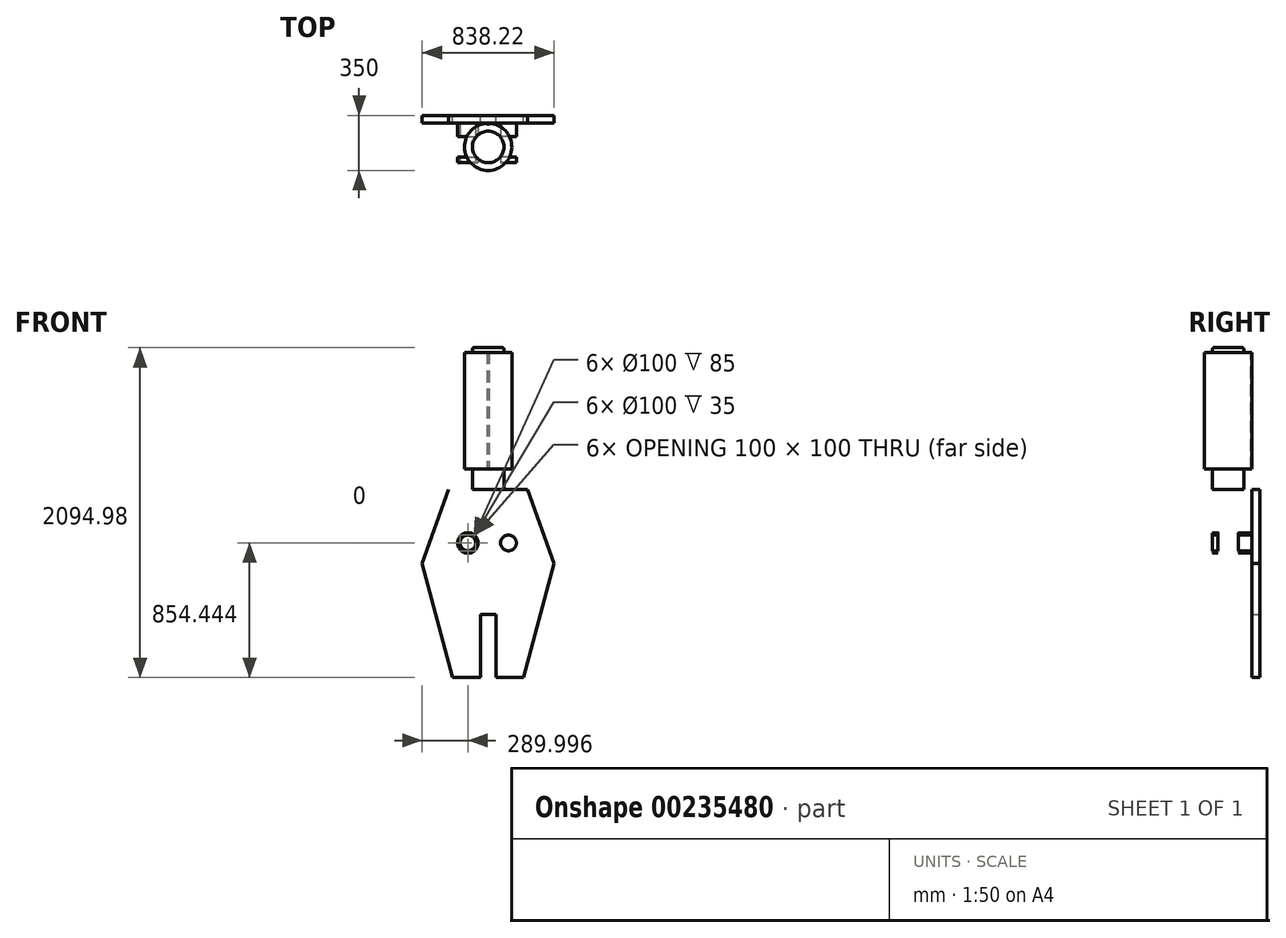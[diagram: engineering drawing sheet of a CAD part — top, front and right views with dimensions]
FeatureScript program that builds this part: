
annotation { "Feature Type Name" : "Feature", "Feature Type Description" : "" }
export const myFeature = defineFeature(function(context is Context, id is Id, definition is map)
    precondition{}
    {
        {
            var Q0;
            Q0=qCreatedBy(makeId("Front.planeOp"),FACE);
            var sketch = newSketch(context, id + "F0", { "sketchPlane" : qUnion([Q0])});
            skLineSegment(sketch, "E0", {"start": v(-250, 794.98) * mm, "end": v(250, 794.98) * mm});
            skLineSegment(sketch, "E1", {"start": v(250, 794.98) * mm, "end": v(419.11, 324.44) * mm});
            skLineSegment(sketch, "E2", {"start": v(419.11, 324.44) * mm, "end": v(225, -400) * mm});
            skLineSegment(sketch, "E3", {"start": v(225, -400) * mm, "end": v(50, -400) * mm});
            skLineSegment(sketch, "E4", {"start": v(-50, -400) * mm, "end": v(-50, 0) * mm});
            skLineSegment(sketch, "E5", {"start": v(0, 0) * mm, "end": v(-50, 0) * mm});
            skLineSegment(sketch, "E6.MirrorCS", {"start": v(-250, 794.98) * mm, "end": v(-419.11, 324.44) * mm});
            skLineSegment(sketch, "E7.MirrorCS", {"start": v(-419.11, 324.44) * mm, "end": v(-225, -400) * mm});
            skLineSegment(sketch, "E8.MirrorCS", {"start": v(-225, -400) * mm, "end": v(-50, -400) * mm});
            skLineSegment(sketch, "E9.MirrorCS", {"start": v(50, -400) * mm, "end": v(50, 0) * mm});
            skLineSegment(sketch, "E10.MirrorCS", {"start": v(0, 0) * mm, "end": v(50, 0) * mm});
            skPoint(sketch, "E11.orphan", {"position": v(50, -400) * mm});
            skSolve(sketch);
        }
        {
            var Q0;
            Q0=makeQuery(id+"F0.imprint","IMPRINT",FACE,{"disambiguationData":[TD([[makeQuery(id+"F0.imprint","IMPRINT",EDGE,{"derivedFrom":sQuery(id+"F0.wireOp",EDGE,"E0")}),-1.0]])]});
            extrude(context, id + "F1", {"entities" : qUnion([Q0]), "endBound" : BoundingType.SYMMETRIC, "depth" : 400 * mm});
        }
        {
            var Q0;
            Q0=makeQuery(id+"F1.opExtrude","SWEPT_FACE",FACE,{"disambiguationData":[OSD([sQuery(id+"F0.wireOp",EDGE,"E0")])]});
            var sketch = newSketch(context, id + "F2", { "sketchPlane" : qUnion([Q0])});
            skCircle(sketch, "E12", {"center": v(0, 0) * mm, "radius": 100 * mm});
            skSolve(sketch);
        }
        {
            var Q0;
            Q0=makeQuery(id+"F2.imprint","IMPRINT",FACE,{"disambiguationData":[TD([[makeQuery(id+"F2.imprint","IMPRINT",EDGE,{"derivedFrom":sQuery(id+"F2.wireOp",EDGE,"E12")}),1.0]])]});
            extrude(context, id + "F3", {"entities" : qUnion([Q0]), "operationType" : NewBodyOperationType.ADD, "depth" : 900 * mm});
        }
        {
            var Q0;
            Q0=makeQuery(id+"F2.imprint","IMPRINT",FACE,{"disambiguationData":[TD([[makeQuery(id+"F2.imprint","IMPRINT",EDGE,{"derivedFrom":sQuery(id+"F2.wireOp",EDGE,"E12")}),-1.0]])]});
            cPlane(context, id + "F4", {"entities" : qUnion([Q0]), "cplaneType" : CPlaneType.OFFSET, "offset" : 130 * mm, "width" : 150 * mm, "height" : 150 * mm});
        }
        {
            var Q0;
            Q0=qCreatedBy(id+"F4.planeOp",FACE);
            var sketch = newSketch(context, id + "F5", { "sketchPlane" : qUnion([Q0])});
            skCircle(sketch, "E13", {"center": v(0, 0) * mm, "radius": 150 * mm});
            skSolve(sketch);
        }
        {
            var Q0;
            Q0 = qSketchRegion(id + "F5", true);
            extrude(context, id + "F6", {"entities" : qUnion([Q0]), "operationType" : NewBodyOperationType.ADD, "depth" : 740 * mm});
        }
        {
            var Q0;
            Q0=qCreatedBy(makeId("Right.planeOp"),FACE);
            var sketch = newSketch(context, id + "F7", { "sketchPlane" : qUnion([Q0])});
            skLineSegment(sketch, "E14.0", {"start": v(200, 324.44) * mm, "end": v(200, -400) * mm, "construction": true});
            skLineSegment(sketch, "E15.0", {"start": v(-200, -400) * mm, "end": v(200, -400) * mm});
            skLineSegment(sketch, "E16.0", {"start": v(-200, 324.44) * mm, "end": v(-200, -400) * mm, "construction": true});
            skLineSegment(sketch, "E17.0", {"start": v(200, 794.98) * mm, "end": v(200, 324.44) * mm, "construction": true});
            skLineSegment(sketch, "E18.0", {"start": v(-200, 794.98) * mm, "end": v(-200, 324.44) * mm, "construction": true});
            skLineSegment(sketch, "E19", {"start": v(150, -400) * mm, "end": v(150, 324.44) * mm});
            skLineSegment(sketch, "E20", {"start": v(200, 324.44) * mm, "end": v(150, 324.44) * mm});
            skLineSegment(sketch, "E21", {"start": v(150, 324.44) * mm, "end": v(65, 324.44) * mm});
            skLineSegment(sketch, "E22", {"start": v(65, 324.44) * mm, "end": v(65, 454.44) * mm});
            skLineSegment(sketch, "E23", {"start": v(0, -725.67) * mm, "end": v(0, 855.5) * mm, "construction": true});
            skPoint(sketch, "E23.startSnap0", {"position": v(0, -400) * mm});
            skLineSegment(sketch, "E24.MirrorCS", {"start": v(-150, -400) * mm, "end": v(-150, 324.44) * mm});
            skLineSegment(sketch, "E25.MirrorCS", {"start": v(-65, 324.44) * mm, "end": v(-65, 454.44) * mm});
            skLineSegment(sketch, "E26.MirrorCS", {"start": v(-150, 324.44) * mm, "end": v(-65, 324.44) * mm});
            skLineSegment(sketch, "E27.MirrorCS", {"start": v(-200, 324.44) * mm, "end": v(-150, 324.44) * mm});
            skLineSegment(sketch, "E28", {"start": v(65, 454.44) * mm, "end": v(-65, 454.44) * mm});
            skSolve(sketch);
        }
        {
            var Q0;
            Q0 = qSketchRegion(id + "F7", true);
            extrude(context, id + "F8", {"entities" : qUnion([Q0]), "operationType" : NewBodyOperationType.REMOVE, "endBound" : BoundingType.SYMMETRIC, "oppositeDirection" : true, "depth" : 1160 * mm});
        }
        {
            var Q0;
            Q0=makeQuery(id+"F1.opExtrude","CAP_FACE",FACE,{"disambiguationData":[OSD([sQuery(id+"F0.wireOp",EDGE,"E0"),sQuery(id+"F0.wireOp",EDGE,"E1"),sQuery(id+"F0.wireOp",EDGE,"E2"),sQuery(id+"F0.wireOp",EDGE,"E3"),sQuery(id+"F0.wireOp",EDGE,"E4"),sQuery(id+"F0.wireOp",EDGE,"E5"),sQuery(id+"F0.wireOp",EDGE,"E6.MirrorCS"),sQuery(id+"F0.wireOp",EDGE,"E7.MirrorCS"),sQuery(id+"F0.wireOp",EDGE,"E8.MirrorCS"),sQuery(id+"F0.wireOp",EDGE,"E9.MirrorCS"),sQuery(id+"F0.wireOp",EDGE,"E10.MirrorCS")])],"isStart":false});
            var sketch = newSketch(context, id + "F9", { "sketchPlane" : qUnion([Q0])});
            skCircle(sketch, "E29", {"center": v(-129.11, 454.44) * mm, "radius": 50 * mm});
            skCircle(sketch, "E30", {"center": v(-129.11, 454.44) * mm, "radius": 65 * mm});
            skCircle(sketch, "E31.MirrorC", {"center": v(129.11, 454.44) * mm, "radius": 50 * mm});
            skCircle(sketch, "E32.MirrorC", {"center": v(129.11, 454.44) * mm, "radius": 65 * mm});
            skSolve(sketch);
        }
        {
            var Q0;
            Q0=makeQuery(id+"F9.imprint","IMPRINT",FACE,{"disambiguationData":[TD([[makeQuery(id+"F9.imprint","IMPRINT",EDGE,{"derivedFrom":sQuery(id+"F9.wireOp",EDGE,"E29")}),-1.0]])]});
            var Q1;
            Q1=makeQuery(id+"F9.imprint","IMPRINT",FACE,{"disambiguationData":[TD([[makeQuery(id+"F9.imprint","IMPRINT",EDGE,{"derivedFrom":sQuery(id+"F9.wireOp",EDGE,"E31.MirrorC")}),1.0]])]});
            extrude(context, id + "F10", {"entities" : qUnion([Q0, Q1]), "operationType" : NewBodyOperationType.REMOVE, "oppositeDirection" : true, "depth" : 100 * mm});
        }
        {
            var Q0;
            Q0=makeQuery(id+"F10.boolean.opBoolean","SPLIT",FACE,{"disambiguationData":[TD([makeQuery(id+"F10.opExtrude","SWEPT_FACE",FACE,{"disambiguationData":[OSD([sQuery(id+"F9.wireOp",EDGE,"E29")])]})])],"derivedFrom":makeQuery(id+"F1.opExtrude","CAP_FACE",FACE,{"disambiguationData":[OSD([sQuery(id+"F0.wireOp",EDGE,"E0"),sQuery(id+"F0.wireOp",EDGE,"E1"),sQuery(id+"F0.wireOp",EDGE,"E2"),sQuery(id+"F0.wireOp",EDGE,"E3"),sQuery(id+"F0.wireOp",EDGE,"E4"),sQuery(id+"F0.wireOp",EDGE,"E5"),sQuery(id+"F0.wireOp",EDGE,"E6.MirrorCS"),sQuery(id+"F0.wireOp",EDGE,"E7.MirrorCS"),sQuery(id+"F0.wireOp",EDGE,"E8.MirrorCS"),sQuery(id+"F0.wireOp",EDGE,"E9.MirrorCS"),sQuery(id+"F0.wireOp",EDGE,"E10.MirrorCS")])],"isStart":false})});
            var Q1;
            Q1=makeQuery(id+"F10.boolean.opBoolean","SPLIT",FACE,{"disambiguationData":[TD([makeQuery(id+"F10.opExtrude","SWEPT_FACE",FACE,{"disambiguationData":[OSD([sQuery(id+"F9.wireOp",EDGE,"E31.MirrorC")])]})])],"derivedFrom":makeQuery(id+"F1.opExtrude","CAP_FACE",FACE,{"disambiguationData":[OSD([sQuery(id+"F0.wireOp",EDGE,"E0"),sQuery(id+"F0.wireOp",EDGE,"E1"),sQuery(id+"F0.wireOp",EDGE,"E2"),sQuery(id+"F0.wireOp",EDGE,"E3"),sQuery(id+"F0.wireOp",EDGE,"E4"),sQuery(id+"F0.wireOp",EDGE,"E5"),sQuery(id+"F0.wireOp",EDGE,"E6.MirrorCS"),sQuery(id+"F0.wireOp",EDGE,"E7.MirrorCS"),sQuery(id+"F0.wireOp",EDGE,"E8.MirrorCS"),sQuery(id+"F0.wireOp",EDGE,"E9.MirrorCS"),sQuery(id+"F0.wireOp",EDGE,"E10.MirrorCS")])],"isStart":false})});
            extrude(context, id + "F11", {"entities" : qUnion([Q0, Q1]), "operationType" : NewBodyOperationType.REMOVE, "oppositeDirection" : true, "depth" : 350 * mm});
        }
        {
            var Q0;
            Q0=qCreatedBy(makeId("Front.planeOp"),FACE);
            var sketch = newSketch(context, id + "F12", { "sketchPlane" : qUnion([Q0])});
            skLineSegment(sketch, "E33", {"start": v(-272.54, 584.44) * mm, "end": v(272.54, 584.44) * mm});
            skLineSegment(sketch, "E34", {"start": v(-272.54, 584.44) * mm, "end": v(-297.7, 514.44) * mm});
            skLineSegment(sketch, "E35.MirrorCS", {"start": v(272.54, 584.44) * mm, "end": v(297.7, 514.44) * mm});
            skCircle(sketch, "E36.0", {"center": v(129.11, 454.44) * mm, "radius": 50 * mm, "construction": true});
            skLineSegment(sketch, "E37.0", {"start": v(-250, 794.98) * mm, "end": v(-419.11, 324.44) * mm, "construction": true});
            skPoint(sketch, "E38", {"position": v(-372.4, 454.44) * mm});
            skPoint(sketch, "E39", {"position": v(-527.75, 839.47) * mm});
            skLineSegment(sketch, "E40", {"start": v(-372.4, 454.44) * mm, "end": v(-297.7, 514.44) * mm});
            skLineSegment(sketch, "E41.MirrorCS", {"start": v(372.4, 454.44) * mm, "end": v(297.7, 514.44) * mm});
            skLineSegment(sketch, "E42", {"start": v(-372.4, 454.44) * mm, "end": v(-419.11, 324.44) * mm});
            skPoint(sketch, "E43.0", {"position": v(419.11, 324.44) * mm});
            skLineSegment(sketch, "E44", {"start": v(-419.11, 324.44) * mm, "end": v(419.11, 324.44) * mm});
            skLineSegment(sketch, "E45", {"start": v(372.4, 454.44) * mm, "end": v(419.11, 324.44) * mm});
            skSolve(sketch);
        }
        {
            var Q0;
            Q0 = qSketchRegion(id + "F12", true);
            extrude(context, id + "F13", {"entities" : qUnion([Q0]), "operationType" : NewBodyOperationType.REMOVE, "endBound" : BoundingType.SYMMETRIC, "depth" : 130 * mm});
        }
        {
            var Q0;
            Q0=makeQuery(id+"F3.opExtrude","CAP_EDGE",EDGE,{"disambiguationData":[OSD([sQuery(id+"F2.wireOp",EDGE,"E12")])],"isStart":false});
            var Q1;
            Q1=makeQuery(id+"F3.opExtrude","CAP_EDGE",EDGE,{"disambiguationData":[OSD([sQuery(id+"F2.wireOp",EDGE,"E12")])],"isStart":true});
            fillet(context, id + "F14", {"entities" : qUnion([Q0, Q1]), "radius" : 10 * mm, "tangentPropagation" : true, "allowEdgeOverflow" : false});
        }
        {
            var Q0;
            Q0=makeQuery(id+"F6.opExtrude","CAP_FACE",FACE,{"disambiguationData":[OSD([sQuery(id+"F5.wireOp",EDGE,"E13")])],"isStart":false});
            var sketch = newSketch(context, id + "F15", { "sketchPlane" : qUnion([Q0])});
            skLineSegment(sketch, "E46.bottom", {"start": v(5.81, 154.74) * mm, "end": v(-5.81, 154.74) * mm});
            skLineSegment(sketch, "E46.top", {"start": v(5.81, 145.26) * mm, "end": v(-5.81, 145.26) * mm});
            skLineSegment(sketch, "E46.left", {"start": v(5.81, 154.74) * mm, "end": v(5.81, 145.26) * mm});
            skLineSegment(sketch, "E46.right", {"start": v(-5.81, 154.74) * mm, "end": v(-5.81, 145.26) * mm});
            skPoint(sketch, "E46.middle", {"position": v(0, 150) * mm});
            skSolve(sketch);
        }
        {
            var Q0;
            Q0 = qSketchRegion(id + "F15", true);
            var Q1;
            Q1=makeQuery(id+"F6.opExtrude","CAP_FACE",FACE,{"disambiguationData":[OSD([sQuery(id+"F5.wireOp",EDGE,"E13")])],"isStart":true});
            extrude(context, id + "F16", {"entities" : qUnion([Q0]), "operationType" : NewBodyOperationType.REMOVE, "endBound" : BoundingType.UP_TO_SURFACE, "oppositeDirection" : true, "endBoundEntityFace" : qUnion([Q1]), "depth" : 25 * mm});
        }
    });
